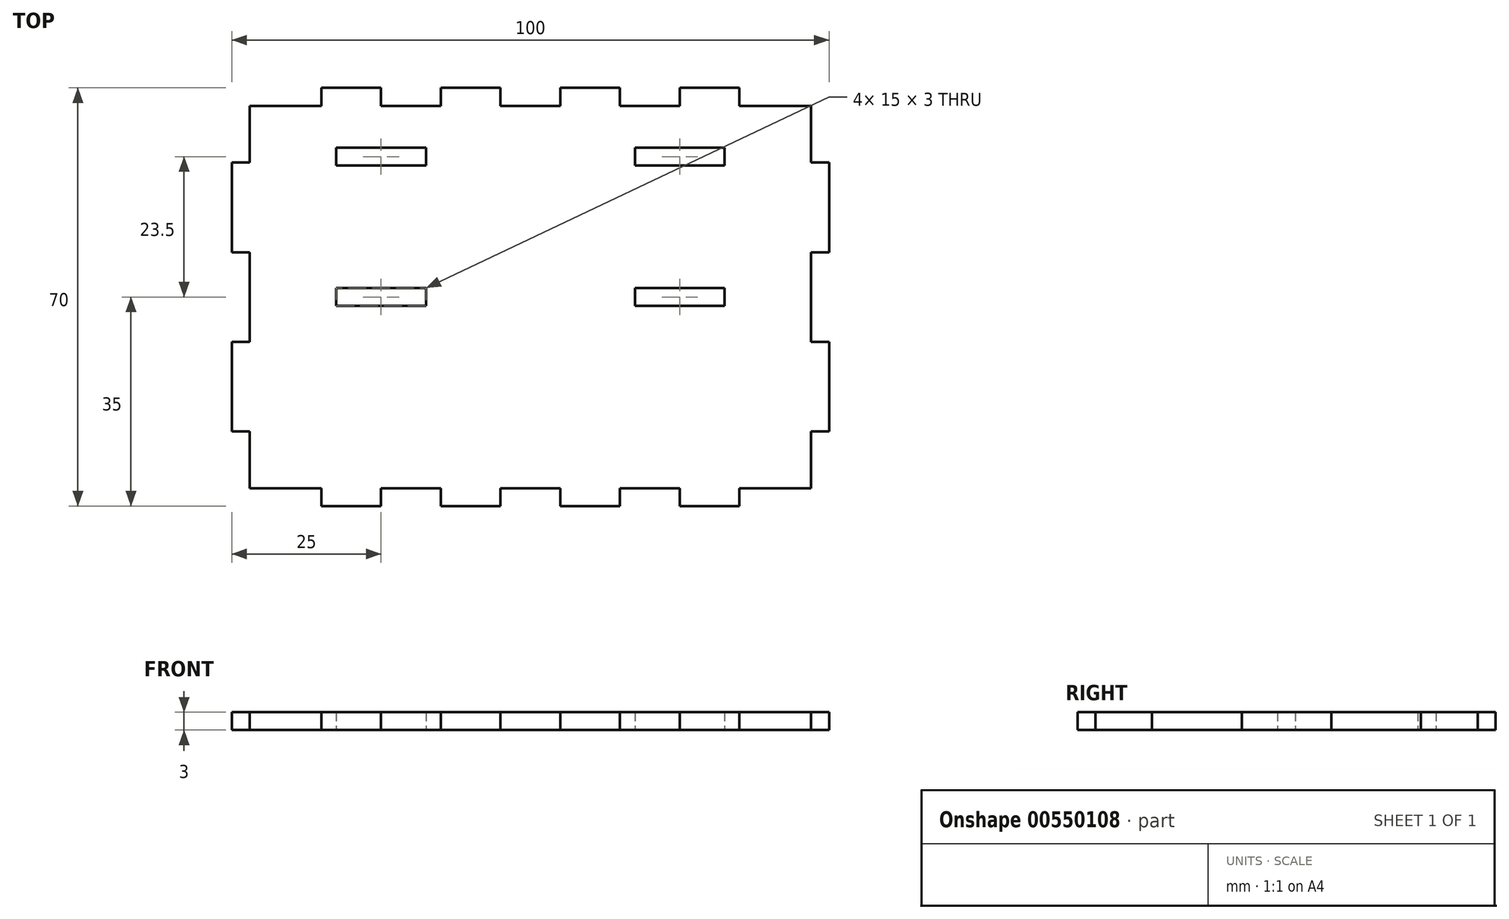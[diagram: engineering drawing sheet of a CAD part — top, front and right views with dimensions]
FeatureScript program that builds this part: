
annotation { "Feature Type Name" : "Feature", "Feature Type Description" : "" }
export const myFeature = defineFeature(function(context is Context, id is Id, definition is map)
    precondition{}
    {
        {
            var Q0;
            Q0=qCreatedBy(makeId("Top.planeOp"),FACE);
            var sketch = newSketch(context, id + "F0", { "sketchPlane" : qUnion([Q0])});
            skLineSegment(sketch, "E0", {"start": v(-47, 32) * mm, "end": v(-35, 32) * mm});
            skLineSegment(sketch, "E1", {"start": v(-35, 32) * mm, "end": v(-35, 35) * mm});
            skLineSegment(sketch, "E2", {"start": v(-35, 35) * mm, "end": v(-25, 35) * mm});
            skLineSegment(sketch, "E3", {"start": v(-25, 35) * mm, "end": v(-25, 32) * mm});
            skLineSegment(sketch, "E4", {"start": v(-25, 32) * mm, "end": v(-15, 32) * mm});
            skLineSegment(sketch, "E5", {"start": v(-15, 32) * mm, "end": v(-15, 35) * mm});
            skLineSegment(sketch, "E6", {"start": v(-15, 35) * mm, "end": v(-5, 35) * mm});
            skLineSegment(sketch, "E7", {"start": v(-5, 35) * mm, "end": v(-5, 32) * mm});
            skLineSegment(sketch, "E8", {"start": v(-5, 32) * mm, "end": v(5, 32) * mm});
            skLineSegment(sketch, "E9", {"start": v(5, 32) * mm, "end": v(5, 35) * mm});
            skLineSegment(sketch, "E10", {"start": v(5, 35) * mm, "end": v(15, 35) * mm});
            skLineSegment(sketch, "E11", {"start": v(15, 35) * mm, "end": v(15, 32) * mm});
            skLineSegment(sketch, "E12", {"start": v(15, 32) * mm, "end": v(25, 32) * mm});
            skLineSegment(sketch, "E13", {"start": v(25, 32) * mm, "end": v(25, 35) * mm});
            skLineSegment(sketch, "E14", {"start": v(25, 35) * mm, "end": v(35, 35) * mm});
            skLineSegment(sketch, "E15", {"start": v(35, 35) * mm, "end": v(35, 32) * mm});
            skLineSegment(sketch, "E16", {"start": v(35, 32) * mm, "end": v(47, 32) * mm});
            skLineSegment(sketch, "E17", {"start": v(47, 32) * mm, "end": v(47, 22.5) * mm});
            skLineSegment(sketch, "E18", {"start": v(47, 22.5) * mm, "end": v(50, 22.5) * mm});
            skLineSegment(sketch, "E19", {"start": v(50, 22.5) * mm, "end": v(50, 7.5) * mm});
            skLineSegment(sketch, "E20", {"start": v(50, 7.5) * mm, "end": v(47, 7.5) * mm});
            skLineSegment(sketch, "E21", {"start": v(47, 7.5) * mm, "end": v(47, -7.5) * mm});
            skLineSegment(sketch, "E22", {"start": v(47, -7.5) * mm, "end": v(50, -7.5) * mm});
            skLineSegment(sketch, "E23", {"start": v(50, -7.5) * mm, "end": v(50, -22.5) * mm});
            skLineSegment(sketch, "E24", {"start": v(50, -22.5) * mm, "end": v(47, -22.5) * mm});
            skLineSegment(sketch, "E25", {"start": v(47, -22.5) * mm, "end": v(47, -32) * mm});
            skLineSegment(sketch, "E26", {"start": v(47, -32) * mm, "end": v(35, -32) * mm});
            skLineSegment(sketch, "E27", {"start": v(35, -32) * mm, "end": v(35, -35) * mm});
            skLineSegment(sketch, "E28", {"start": v(35, -35) * mm, "end": v(25, -35) * mm});
            skLineSegment(sketch, "E29", {"start": v(25, -35) * mm, "end": v(25, -32) * mm});
            skLineSegment(sketch, "E30", {"start": v(25, -32) * mm, "end": v(15, -32) * mm});
            skLineSegment(sketch, "E31", {"start": v(15, -32) * mm, "end": v(15, -35) * mm});
            skLineSegment(sketch, "E32", {"start": v(15, -35) * mm, "end": v(5, -35) * mm});
            skLineSegment(sketch, "E33", {"start": v(5, -35) * mm, "end": v(5, -32) * mm});
            skLineSegment(sketch, "E34", {"start": v(5, -32) * mm, "end": v(-5, -32) * mm});
            skLineSegment(sketch, "E35", {"start": v(-5, -32) * mm, "end": v(-5, -35) * mm});
            skLineSegment(sketch, "E36", {"start": v(-5, -35) * mm, "end": v(-15, -35) * mm});
            skLineSegment(sketch, "E37", {"start": v(-15, -35) * mm, "end": v(-15, -32) * mm});
            skLineSegment(sketch, "E38", {"start": v(-15, -32) * mm, "end": v(-25, -32) * mm});
            skLineSegment(sketch, "E39", {"start": v(-25, -32) * mm, "end": v(-25, -35) * mm});
            skLineSegment(sketch, "E40", {"start": v(-25, -35) * mm, "end": v(-35, -35) * mm});
            skLineSegment(sketch, "E41", {"start": v(-35, -35) * mm, "end": v(-35, -32) * mm});
            skLineSegment(sketch, "E42", {"start": v(-35, -32) * mm, "end": v(-47, -32) * mm});
            skLineSegment(sketch, "E43", {"start": v(-47, -32) * mm, "end": v(-47, -22.5) * mm});
            skLineSegment(sketch, "E44", {"start": v(-47, -22.5) * mm, "end": v(-50, -22.5) * mm});
            skLineSegment(sketch, "E45", {"start": v(-50, -22.5) * mm, "end": v(-50, -7.5) * mm});
            skLineSegment(sketch, "E46", {"start": v(-50, -7.5) * mm, "end": v(-47, -7.5) * mm});
            skLineSegment(sketch, "E47", {"start": v(-47, -7.5) * mm, "end": v(-47, 7.5) * mm});
            skLineSegment(sketch, "E48", {"start": v(-47, 7.5) * mm, "end": v(-50, 7.5) * mm});
            skLineSegment(sketch, "E49", {"start": v(-50, 7.5) * mm, "end": v(-50, 22.5) * mm});
            skLineSegment(sketch, "E50", {"start": v(-50, 22.5) * mm, "end": v(-47, 22.5) * mm});
            skLineSegment(sketch, "E51", {"start": v(-47, 22.5) * mm, "end": v(-47, 32) * mm});
            skLineSegment(sketch, "E52", {"start": v(-47, -32) * mm, "end": v(47, 32) * mm, "construction": true});
            skLineSegment(sketch, "E53.bottom", {"start": v(-32.5, 22) * mm, "end": v(-17.5, 22) * mm});
            skLineSegment(sketch, "E53.top", {"start": v(-32.5, 25) * mm, "end": v(-17.5, 25) * mm});
            skLineSegment(sketch, "E53.left", {"start": v(-32.5, 22) * mm, "end": v(-32.5, 25) * mm});
            skLineSegment(sketch, "E53.right", {"start": v(-17.5, 22) * mm, "end": v(-17.5, 25) * mm});
            skLineSegment(sketch, "E54.bottom", {"start": v(17.5, 22) * mm, "end": v(32.5, 22) * mm});
            skLineSegment(sketch, "E54.top", {"start": v(17.5, 25) * mm, "end": v(32.5, 25) * mm});
            skLineSegment(sketch, "E54.left", {"start": v(17.5, 22) * mm, "end": v(17.5, 25) * mm});
            skLineSegment(sketch, "E54.right", {"start": v(32.5, 22) * mm, "end": v(32.5, 25) * mm});
            skLineSegment(sketch, "E55.bottom", {"start": v(-32.5, 1.5) * mm, "end": v(-17.5, 1.5) * mm});
            skLineSegment(sketch, "E55.top", {"start": v(-32.5, -1.5) * mm, "end": v(-17.5, -1.5) * mm});
            skLineSegment(sketch, "E55.left", {"start": v(-32.5, 1.5) * mm, "end": v(-32.5, -1.5) * mm});
            skLineSegment(sketch, "E55.right", {"start": v(-17.5, 1.5) * mm, "end": v(-17.5, -1.5) * mm});
            skLineSegment(sketch, "E56.bottom", {"start": v(17.5, 1.5) * mm, "end": v(32.5, 1.5) * mm});
            skLineSegment(sketch, "E56.top", {"start": v(17.5, -1.5) * mm, "end": v(32.5, -1.5) * mm});
            skLineSegment(sketch, "E56.left", {"start": v(17.5, 1.5) * mm, "end": v(17.5, -1.5) * mm});
            skLineSegment(sketch, "E56.right", {"start": v(32.5, 1.5) * mm, "end": v(32.5, -1.5) * mm});
            skPoint(sketch, "E57", {"position": v(0, 0) * mm});
            skPoint(sketch, "E58", {"position": v(17.5, 0) * mm});
            skPoint(sketch, "E59", {"position": v(-17.5, 0) * mm});
            skSolve(sketch);
        }
        {
            var Q0;
            Q0=makeQuery(id+"F0.imprint","IMPRINT",FACE,{"disambiguationData":[TD([[makeQuery(id+"F0.imprint","IMPRINT",EDGE,{"derivedFrom":sQuery(id+"F0.wireOp",EDGE,"E0")}),-1.0]])]});
            extrude(context, id + "F1", {"entities" : qUnion([Q0]), "depth" : 3 * mm, "offsetDistance" : 25 * mm});
        }
    });
